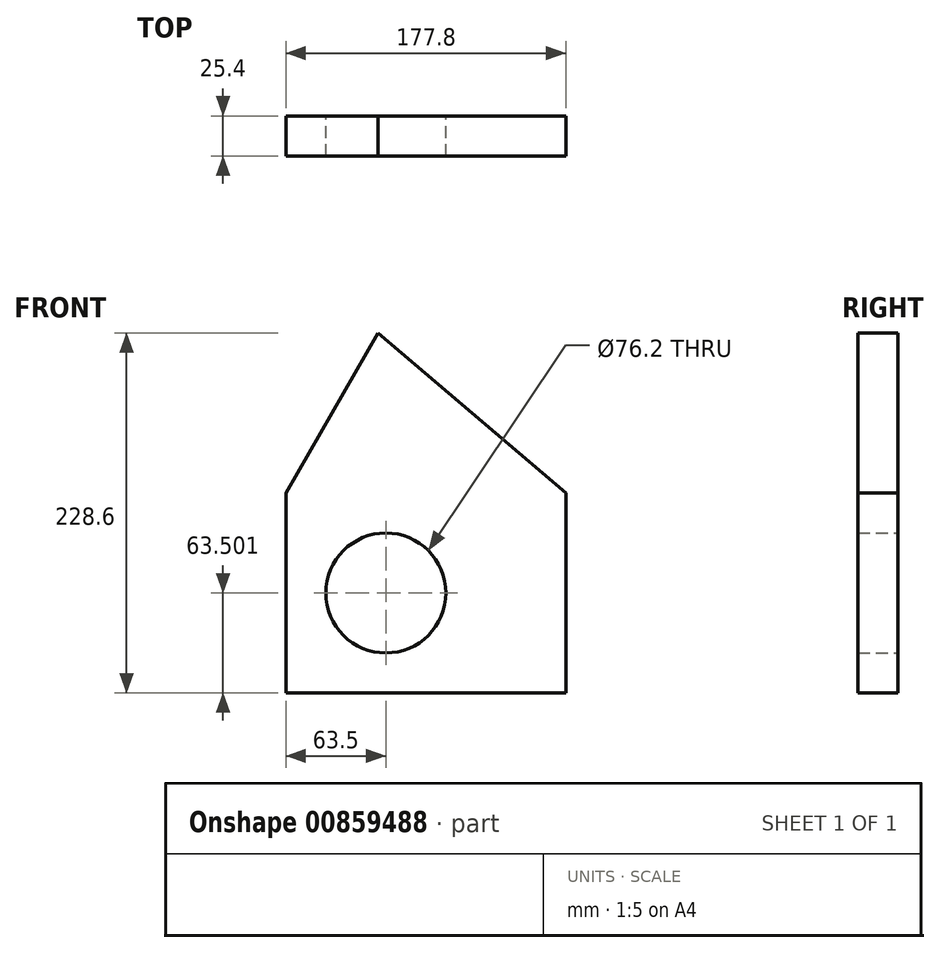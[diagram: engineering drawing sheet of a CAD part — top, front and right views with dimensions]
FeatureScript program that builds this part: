
annotation { "Feature Type Name" : "Feature", "Feature Type Description" : "" }
export const myFeature = defineFeature(function(context is Context, id is Id, definition is map)
    precondition{}
    {
        {
            var Q0;
            Q0=qCreatedBy(makeId("Front.planeOp"),FACE);
            var sketch = newSketch(context, id + "F0", { "sketchPlane" : qUnion([Q0])});
            skLineSegment(sketch, "E0.bottom", {"start": v(114.3, 10.1) * mm, "end": v(-63.5, 10.1) * mm});
            skLineSegment(sketch, "E0.top", {"start": v(114.3, -116.9) * mm, "end": v(-63.5, -116.9) * mm});
            skLineSegment(sketch, "E0.left", {"start": v(114.3, 10.1) * mm, "end": v(114.3, -116.9) * mm});
            skLineSegment(sketch, "E0.right", {"start": v(-63.5, 10.1) * mm, "end": v(-63.5, -116.9) * mm});
            skLineSegment(sketch, "E1", {"start": v(114.3, 10.1) * mm, "end": v(-4.84, 111.7) * mm});
            skLineSegment(sketch, "E2", {"start": v(-4.84, 111.7) * mm, "end": v(-63.5, 10.1) * mm});
            skCircle(sketch, "E3", {"center": v(0, -53.4) * mm, "radius": 38.1 * mm});
            skSolve(sketch);
        }
        {
            var Q0;
            Q0 = qSketchRegion(id + "F0", true);
            extrude(context, id + "F1", {"entities" : qUnion([Q0]), "depth" : 25.4 * mm, "offsetDistance" : 25.4 * mm});
        }
    });
